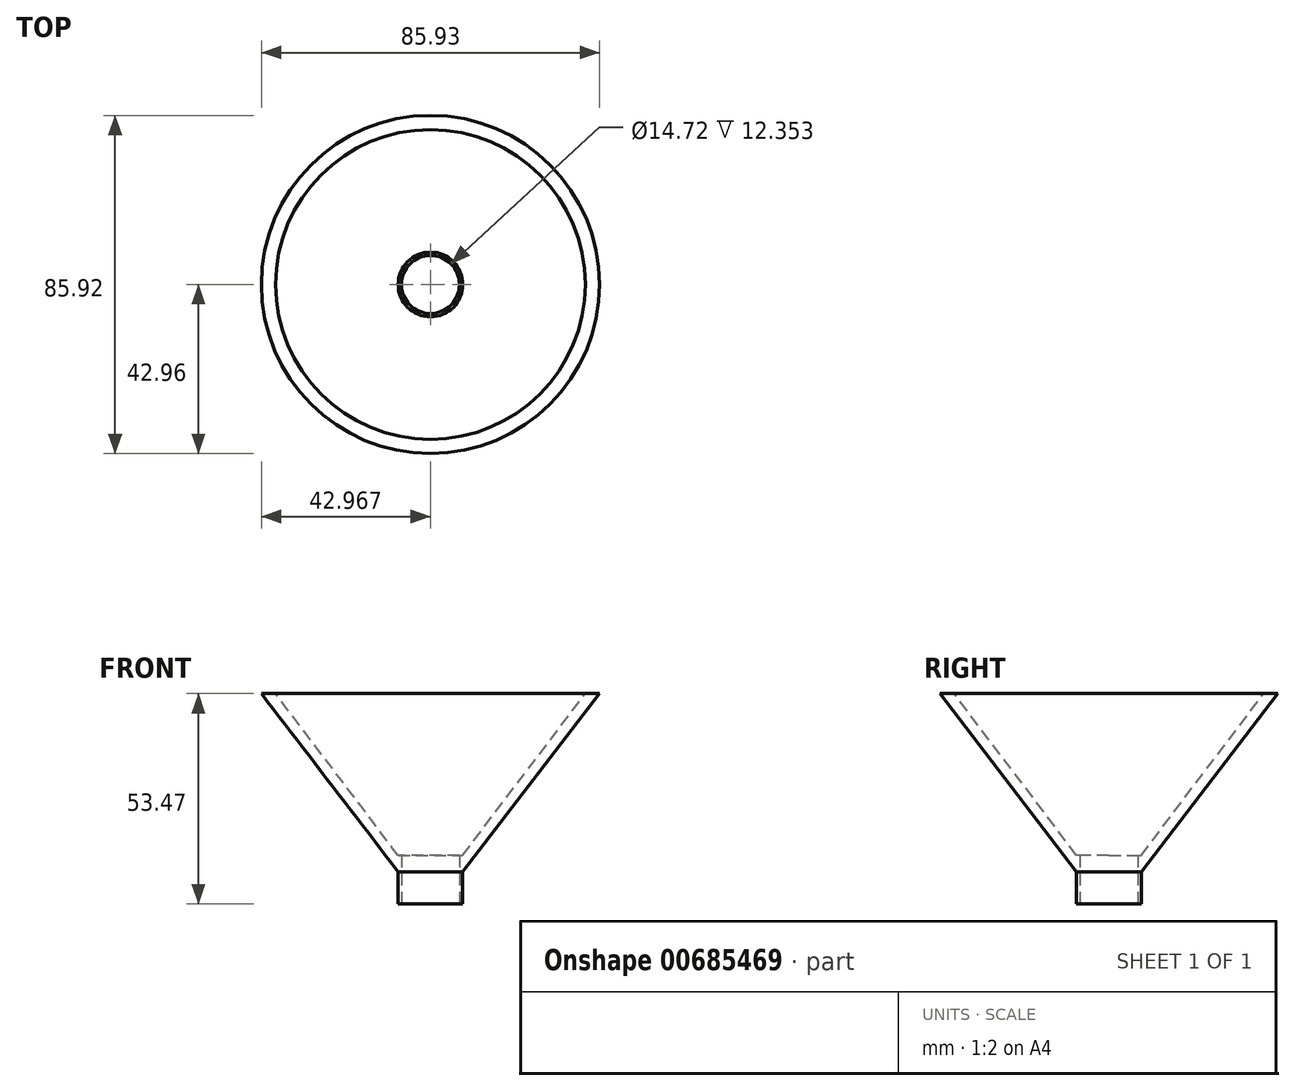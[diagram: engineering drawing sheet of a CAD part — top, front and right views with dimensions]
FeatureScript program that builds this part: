
annotation { "Feature Type Name" : "Feature", "Feature Type Description" : "" }
export const myFeature = defineFeature(function(context is Context, id is Id, definition is map)
    precondition{}
    {
        {
            var Q0;
            Q0=qCreatedBy(makeId("Front.planeOp"),FACE);
            var sketch = newSketch(context, id + "F0", { "sketchPlane" : qUnion([Q0])});
            skLineSegment(sketch, "E0", {"start": v(6.59, 6.4) * mm, "end": v(37.71, 47.45) * mm});
            skLineSegment(sketch, "E1", {"start": v(37.71, 47.45) * mm, "end": v(41.34, 47.45) * mm});
            skLineSegment(sketch, "E2", {"start": v(41.34, 47.45) * mm, "end": v(6.59, 2.2) * mm});
            skLineSegment(sketch, "E3", {"start": v(6.59, 2.2) * mm, "end": v(6.59, -6.02) * mm});
            skLineSegment(sketch, "E4", {"start": v(6.59, -6.02) * mm, "end": v(-1.62, -6.02) * mm});
            skLineSegment(sketch, "E5", {"start": v(-1.62, -6.02) * mm, "end": v(-1.62, 5.82) * mm});
            skLineSegment(sketch, "E6", {"start": v(-1.62, 5.82) * mm, "end": v(6.59, 6.4) * mm});
            skSolve(sketch);
        }
        {
            var Q0;
            Q0=makeQuery(id+"F0.imprint","IMPRINT",FACE,{"disambiguationData":[TD([[makeQuery(id+"F0.imprint","IMPRINT",EDGE,{"derivedFrom":sQuery(id+"F0.wireOp",EDGE,"E0")}),-1.0]])]});
            var Q1;
            Q1=sQuery(id+"F0.wireOp",EDGE,"E5");
            revolve(context, id + "F1", {"entities" : qUnion([Q0]), "axis" : qUnion([Q1]), "revolveType" : RevolveType.FULL});
        }
        {
            var Q0;
            Q0=makeQuery(id+"F1.opRevolve","SWEPT_FACE",FACE,{"disambiguationData":[OSD([sQuery(id+"F0.wireOp",EDGE,"E4")])]});
            var sketch = newSketch(context, id + "F2", { "sketchPlane" : qUnion([Q0])});
            skCircle(sketch, "E7", {"center": v(-1.62, 0) * mm, "radius": 8.3 * mm});
            skCircle(sketch, "E8", {"center": v(-1.62, 0) * mm, "radius": 7.36 * mm});
            skSolve(sketch);
        }
        {
            var Q0;
            Q0=makeQuery(id+"F2.imprint","IMPRINT",FACE,{"disambiguationData":[TD([[makeQuery(id+"F2.imprint","IMPRINT",EDGE,{"derivedFrom":sQuery(id+"F2.wireOp",EDGE,"E8")}),1.0]])]});
            extrude(context, id + "F3", {"entities" : qUnion([Q0]), "operationType" : NewBodyOperationType.REMOVE, "oppositeDirection" : true, "depth" : 25.4 * mm, "offsetDistance" : 25.4 * mm});
        }
    });
